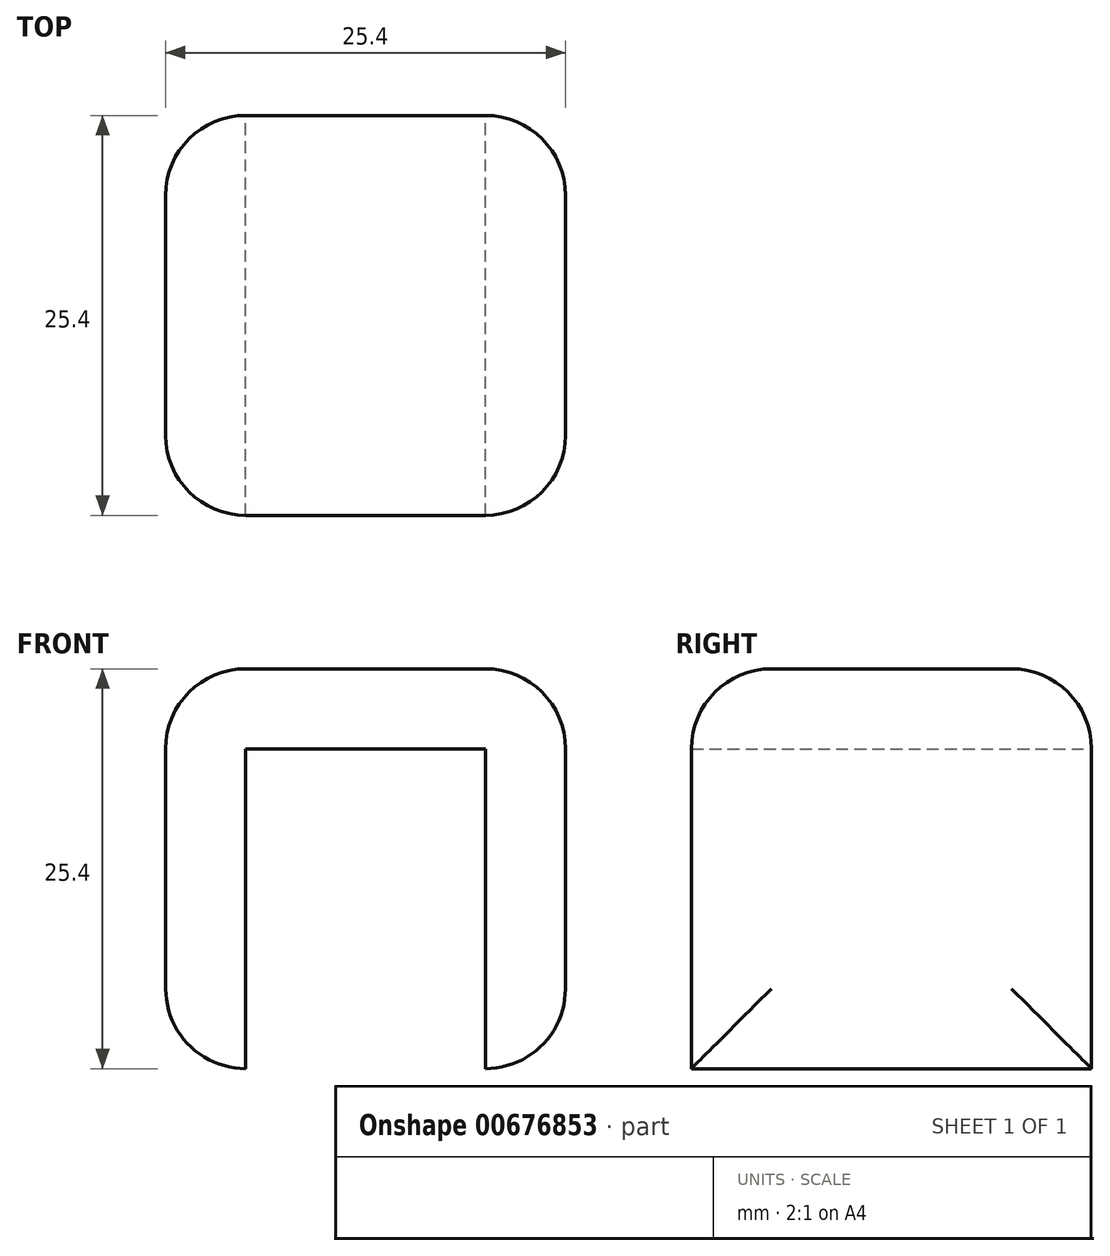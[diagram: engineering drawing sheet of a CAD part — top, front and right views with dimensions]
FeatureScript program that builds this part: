
annotation { "Feature Type Name" : "Feature", "Feature Type Description" : "" }
export const myFeature = defineFeature(function(context is Context, id is Id, definition is map)
    precondition{}
    {
        {
            var Q0;
            Q0=qCreatedBy(makeId("Front.planeOp"),FACE);
            var sketch = newSketch(context, id + "F0", { "sketchPlane" : qUnion([Q0])});
            skLineSegment(sketch, "E0.bottom", {"start": v(0, 0) * mm, "end": v(25.4, 0) * mm});
            skLineSegment(sketch, "E0.top", {"start": v(0, -25.4) * mm, "end": v(25.4, -25.4) * mm});
            skLineSegment(sketch, "E0.left", {"start": v(0, 0) * mm, "end": v(0, -25.4) * mm});
            skLineSegment(sketch, "E0.right", {"start": v(25.4, 0) * mm, "end": v(25.4, -25.4) * mm});
            skLineSegment(sketch, "E1.bottom", {"start": v(5.08, -25.4) * mm, "end": v(20.32, -25.4) * mm});
            skLineSegment(sketch, "E1.top", {"start": v(5.08, -5.08) * mm, "end": v(20.32, -5.08) * mm});
            skLineSegment(sketch, "E1.left", {"start": v(5.08, -25.4) * mm, "end": v(5.08, -5.08) * mm});
            skLineSegment(sketch, "E1.right", {"start": v(20.32, -25.4) * mm, "end": v(20.32, -5.08) * mm});
            skSolve(sketch);
        }
        {
            var Q0;
            Q0=makeQuery(id+"F0.imprint","IMPRINT",FACE,{"disambiguationData":[TD([[makeQuery(id+"F0.imprint","IMPRINT",EDGE,{"derivedFrom":sQuery(id+"F0.wireOp",EDGE,"E0.bottom")}),-1.0]])]});
            extrude(context, id + "F1", {"entities" : qUnion([Q0]), "depth" : 25.4 * mm, "offsetDistance" : 25.4 * mm});
        }
        {
            var Q0;
            Q0=makeQuery(id+"F1.opExtrude","SWEPT_EDGE",EDGE,{"disambiguationData":[OSD([sQuery(id+"F0.wireOp",EDGE,"E0.bottom"),sQuery(id+"F0.wireOp",EDGE,"E0.left")])]});
            var Q1;
            Q1=makeQuery(id+"F1.opExtrude","CAP_EDGE",EDGE,{"disambiguationData":[OSD([sQuery(id+"F0.wireOp",EDGE,"E0.bottom")])],"isStart":false});
            var Q2;
            Q2=makeQuery(id+"F1.opExtrude","SWEPT_EDGE",EDGE,{"disambiguationData":[OSD([sQuery(id+"F0.wireOp",EDGE,"E0.bottom"),sQuery(id+"F0.wireOp",EDGE,"E0.right")])]});
            var Q3;
            Q3=makeQuery(id+"F1.opExtrude","CAP_EDGE",EDGE,{"disambiguationData":[OSD([sQuery(id+"F0.wireOp",EDGE,"E0.bottom")])],"isStart":true});
            var Q4;
            Q4=makeQuery(id+"F1.opExtrude","CAP_EDGE",EDGE,{"disambiguationData":[OSD([sQuery(id+"F0.wireOp",EDGE,"E0.left")])],"isStart":false});
            var Q5;
            Q5=makeQuery(id+"F1.opExtrude","CAP_EDGE",EDGE,{"disambiguationData":[OSD([sQuery(id+"F0.wireOp",EDGE,"E0.left")])],"isStart":true});
            var Q6;
            Q6=makeQuery(id+"F1.opExtrude","CAP_EDGE",EDGE,{"disambiguationData":[OSD([sQuery(id+"F0.wireOp",EDGE,"E0.right")])],"isStart":true});
            var Q7;
            Q7=makeQuery(id+"F1.opExtrude","CAP_EDGE",EDGE,{"disambiguationData":[OSD([sQuery(id+"F0.wireOp",EDGE,"E0.right")])],"isStart":false});
            var Q8;
            Q8=makeQuery(id+"F1.opExtrude","SWEPT_EDGE",EDGE,{"disambiguationData":[OSD([sQuery(id+"F0.wireOp",EDGE,"E0.top"),sQuery(id+"F0.wireOp",EDGE,"E0.left")])]});
            var Q9;
            Q9=makeQuery(id+"F1.opExtrude","SWEPT_EDGE",EDGE,{"disambiguationData":[OSD([sQuery(id+"F0.wireOp",EDGE,"E0.top"),sQuery(id+"F0.wireOp",EDGE,"E0.right")])]});
            fillet(context, id + "F2", {"entities" : qUnion([Q0, Q1, Q2, Q3, Q4, Q5, Q6, Q7, Q8, Q9]), "radius" : 5.08 * mm, "tangentPropagation" : true, "allowEdgeOverflow" : false});
        }
    });
